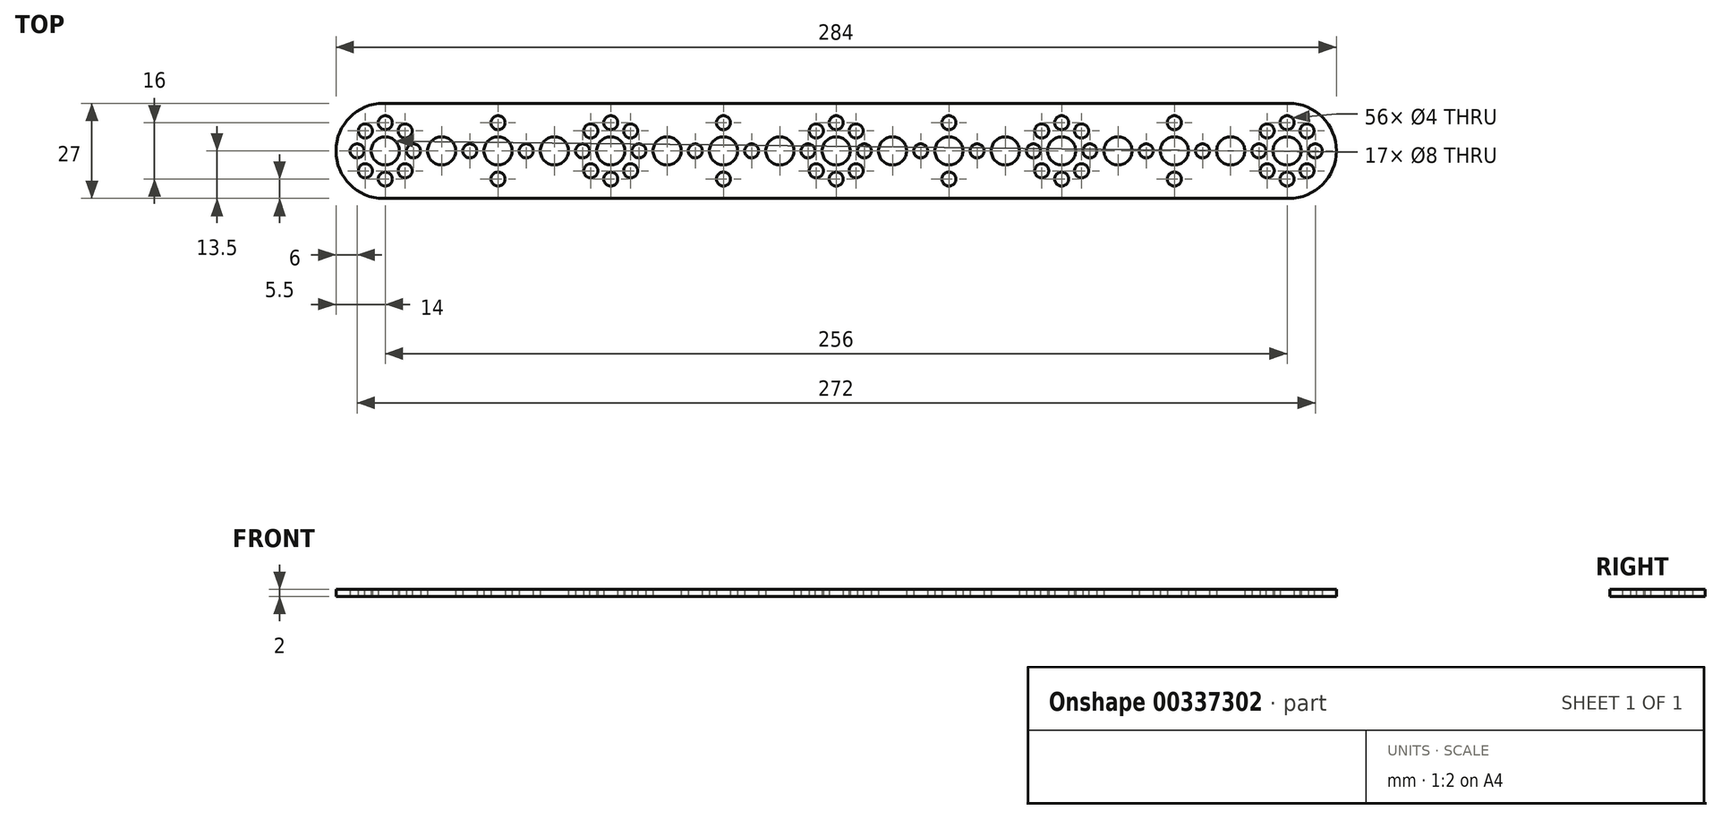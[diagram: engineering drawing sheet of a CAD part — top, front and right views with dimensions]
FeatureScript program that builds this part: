
annotation { "Feature Type Name" : "Feature", "Feature Type Description" : "" }
export const myFeature = defineFeature(function(context is Context, id is Id, definition is map)
    precondition{}
    {
        {
            var Q0;
            Q0=qCreatedBy(makeId("Top.planeOp"),FACE);
            var sketch = newSketch(context, id + "F0", { "sketchPlane" : qUnion([Q0])});
            skLineSegment(sketch, "E0.bottom", {"start": v(128.5, 13.5) * mm, "end": v(-128.5, 13.5) * mm});
            skLineSegment(sketch, "E0.top", {"start": v(128.5, -13.5) * mm, "end": v(-128.5, -13.5) * mm});
            skLineSegment(sketch, "E0.left", {"start": v(128.5, 13.5) * mm, "end": v(128.5, -13.5) * mm});
            skLineSegment(sketch, "E0.right", {"start": v(-128.5, 13.5) * mm, "end": v(-128.5, -13.5) * mm});
            skPoint(sketch, "E0.middle", {"position": v(0, 0) * mm});
            skArc(sketch, "E1", {"start": v(-128.5, 13.5) * mm, "mid": v(-142, 0) * mm, "end": v(-128.5, -13.5) * mm});
            skArc(sketch, "E2", {"start": v(128.5, -13.5) * mm, "mid": v(142, 0) * mm, "end": v(128.5, 13.5) * mm});
            skLineSegment(sketch, "E3", {"start": v(-128, 2.64) * mm, "end": v(-128, 0) * mm});
            skLineSegment(sketch, "E4", {"start": v(-128, 0) * mm, "end": v(-128, -2.64) * mm});
            skLineSegment(sketch, "E5", {"start": v(-132, 0) * mm, "end": v(-128, 0) * mm});
            skLineSegment(sketch, "E6", {"start": v(-126.43, 0) * mm, "end": v(-128, 0) * mm});
            skLineSegment(sketch, "E7", {"start": v(-128, 0) * mm, "end": v(-126.72, 1.28) * mm});
            skLineSegment(sketch, "E8", {"start": v(-128, 0) * mm, "end": v(-129.4, -1.4) * mm});
            skLineSegment(sketch, "E9", {"start": v(-128, 0) * mm, "end": v(-129.4, 1.4) * mm});
            skLineSegment(sketch, "E10", {"start": v(-128, 0) * mm, "end": v(-126.62, -1.38) * mm});
            skCircle(sketch, "E11", {"center": v(-128, 0) * mm, "radius": 4 * mm});
            skCircle(sketch, "E12", {"center": v(-133.66, 5.66) * mm, "radius": 2 * mm});
            skCircle(sketch, "E13", {"center": v(-128, 8) * mm, "radius": 2 * mm});
            skCircle(sketch, "E14", {"center": v(-122.34, 5.66) * mm, "radius": 2 * mm});
            skCircle(sketch, "E15", {"center": v(-120, 0) * mm, "radius": 2 * mm});
            skCircle(sketch, "E16", {"center": v(-136, 0) * mm, "radius": 2 * mm});
            skCircle(sketch, "E17", {"center": v(-133.66, -5.66) * mm, "radius": 2 * mm});
            skCircle(sketch, "E18", {"center": v(-128, -8) * mm, "radius": 2 * mm});
            skCircle(sketch, "E19", {"center": v(-122.34, -5.66) * mm, "radius": 2 * mm});
            skCircle(sketch, "E20", {"center": v(-112, 0) * mm, "radius": 4 * mm});
            skCircle(sketch, "E21", {"center": v(-96, 0) * mm, "radius": 4 * mm});
            skCircle(sketch, "E22", {"center": v(-96, 8) * mm, "radius": 2 * mm});
            skCircle(sketch, "E23", {"center": v(-88, 0) * mm, "radius": 2 * mm});
            skCircle(sketch, "E24", {"center": v(-96, -8) * mm, "radius": 2 * mm});
            skCircle(sketch, "E25", {"center": v(-104, 0) * mm, "radius": 2 * mm});
            skCircle(sketch, "E26", {"center": v(-80, 0) * mm, "radius": 4 * mm});
            skLineSegment(sketch, "E27", {"start": v(-64, 2.64) * mm, "end": v(-64, 0) * mm});
            skLineSegment(sketch, "E28", {"start": v(-64, 0) * mm, "end": v(-64, -2.64) * mm});
            skLineSegment(sketch, "E29", {"start": v(-65.19, 0) * mm, "end": v(-64, 0) * mm});
            skLineSegment(sketch, "E30", {"start": v(-59.62, 0) * mm, "end": v(-64, 0) * mm});
            skLineSegment(sketch, "E31", {"start": v(-64, 0) * mm, "end": v(-62.72, 1.28) * mm});
            skLineSegment(sketch, "E32", {"start": v(-64, 0) * mm, "end": v(-65.4, -1.4) * mm});
            skLineSegment(sketch, "E33", {"start": v(-64, 0) * mm, "end": v(-65.4, 1.4) * mm});
            skLineSegment(sketch, "E34", {"start": v(-64, 0) * mm, "end": v(-62.62, -1.38) * mm});
            skCircle(sketch, "E35", {"center": v(-64, 0) * mm, "radius": 4 * mm});
            skCircle(sketch, "E36", {"center": v(-69.66, 5.66) * mm, "radius": 2 * mm});
            skCircle(sketch, "E37", {"center": v(-64, 8) * mm, "radius": 2 * mm});
            skCircle(sketch, "E38", {"center": v(-58.34, 5.66) * mm, "radius": 2 * mm});
            skCircle(sketch, "E39", {"center": v(-56, 0) * mm, "radius": 2 * mm});
            skCircle(sketch, "E40", {"center": v(-72, 0) * mm, "radius": 2 * mm});
            skCircle(sketch, "E41", {"center": v(-69.66, -5.66) * mm, "radius": 2 * mm});
            skCircle(sketch, "E42", {"center": v(-64, -8) * mm, "radius": 2 * mm});
            skCircle(sketch, "E43", {"center": v(-58.34, -5.66) * mm, "radius": 2 * mm});
            skCircle(sketch, "E44", {"center": v(-48, 0) * mm, "radius": 4 * mm});
            skCircle(sketch, "E45", {"center": v(-32, 0) * mm, "radius": 4 * mm});
            skCircle(sketch, "E46", {"center": v(-32, 8) * mm, "radius": 2 * mm});
            skCircle(sketch, "E47", {"center": v(-24, 0) * mm, "radius": 2 * mm});
            skCircle(sketch, "E48", {"center": v(-32, -8) * mm, "radius": 2 * mm});
            skCircle(sketch, "E49", {"center": v(-40, 0) * mm, "radius": 2 * mm});
            skCircle(sketch, "E50", {"center": v(-16, 0) * mm, "radius": 4 * mm});
            skCircle(sketch, "E51.MirrorC", {"center": v(16, 0) * mm, "radius": 4 * mm});
            skCircle(sketch, "E52.MirrorC", {"center": v(24, 0) * mm, "radius": 2 * mm});
            skCircle(sketch, "E53.MirrorC", {"center": v(32, 0) * mm, "radius": 4 * mm});
            skCircle(sketch, "E54.MirrorC", {"center": v(32, 8) * mm, "radius": 2 * mm});
            skCircle(sketch, "E55.MirrorC", {"center": v(40, 0) * mm, "radius": 2 * mm});
            skCircle(sketch, "E56.MirrorC", {"center": v(32, -8) * mm, "radius": 2 * mm});
            skCircle(sketch, "E57.MirrorC", {"center": v(48, 0) * mm, "radius": 4 * mm});
            skCircle(sketch, "E58.MirrorC", {"center": v(64, -8) * mm, "radius": 2 * mm});
            skCircle(sketch, "E59.MirrorC", {"center": v(58.34, -5.66) * mm, "radius": 2 * mm});
            skCircle(sketch, "E60.MirrorC", {"center": v(56, 0) * mm, "radius": 2 * mm});
            skCircle(sketch, "E61.MirrorC", {"center": v(58.34, 5.66) * mm, "radius": 2 * mm});
            skCircle(sketch, "E62.MirrorC", {"center": v(64, 8) * mm, "radius": 2 * mm});
            skCircle(sketch, "E63.MirrorC", {"center": v(69.66, 5.66) * mm, "radius": 2 * mm});
            skCircle(sketch, "E64.MirrorC", {"center": v(72, 0) * mm, "radius": 2 * mm});
            skCircle(sketch, "E65.MirrorC", {"center": v(69.66, -5.66) * mm, "radius": 2 * mm});
            skCircle(sketch, "E66.MirrorC", {"center": v(64, 0) * mm, "radius": 4 * mm});
            skCircle(sketch, "E67.MirrorC", {"center": v(80, 0) * mm, "radius": 4 * mm});
            skCircle(sketch, "E68.MirrorC", {"center": v(88, 0) * mm, "radius": 2 * mm});
            skCircle(sketch, "E69.MirrorC", {"center": v(96, 0) * mm, "radius": 4 * mm});
            skCircle(sketch, "E70.MirrorC", {"center": v(96, -8) * mm, "radius": 2 * mm});
            skCircle(sketch, "E71.MirrorC", {"center": v(96, 8) * mm, "radius": 2 * mm});
            skCircle(sketch, "E72.MirrorC", {"center": v(104, 0) * mm, "radius": 2 * mm});
            skCircle(sketch, "E73.MirrorC", {"center": v(112, 0) * mm, "radius": 4 * mm});
            skCircle(sketch, "E74.MirrorC", {"center": v(128, -8) * mm, "radius": 2 * mm});
            skCircle(sketch, "E75.MirrorC", {"center": v(122.34, -5.66) * mm, "radius": 2 * mm});
            skCircle(sketch, "E76.MirrorC", {"center": v(120, 0) * mm, "radius": 2 * mm});
            skCircle(sketch, "E77.MirrorC", {"center": v(122.34, 5.66) * mm, "radius": 2 * mm});
            skCircle(sketch, "E78.MirrorC", {"center": v(128, 8) * mm, "radius": 2 * mm});
            skCircle(sketch, "E79.MirrorC", {"center": v(133.66, 5.66) * mm, "radius": 2 * mm});
            skCircle(sketch, "E80.MirrorC", {"center": v(133.66, -5.66) * mm, "radius": 2 * mm});
            skCircle(sketch, "E81.MirrorC", {"center": v(128, 0) * mm, "radius": 4 * mm});
            skCircle(sketch, "E82.MirrorC", {"center": v(136, 0) * mm, "radius": 2 * mm});
            skLineSegment(sketch, "E83", {"start": v(0, 2.64) * mm, "end": v(0, 0) * mm});
            skLineSegment(sketch, "E84", {"start": v(0, 0) * mm, "end": v(0, -2.64) * mm});
            skLineSegment(sketch, "E85", {"start": v(-1.19, 0) * mm, "end": v(0, 0) * mm});
            skLineSegment(sketch, "E86", {"start": v(4.38, 0) * mm, "end": v(0, 0) * mm});
            skLineSegment(sketch, "E87", {"start": v(0, 0) * mm, "end": v(1.28, 1.28) * mm});
            skLineSegment(sketch, "E88", {"start": v(0, 0) * mm, "end": v(-1.4, -1.4) * mm});
            skLineSegment(sketch, "E89", {"start": v(0, 0) * mm, "end": v(-1.4, 1.4) * mm});
            skLineSegment(sketch, "E90", {"start": v(0, 0) * mm, "end": v(1.38, -1.38) * mm});
            skCircle(sketch, "E91", {"center": v(0, 0) * mm, "radius": 4 * mm});
            skCircle(sketch, "E92", {"center": v(-5.66, 5.66) * mm, "radius": 2 * mm});
            skCircle(sketch, "E93", {"center": v(0, 8) * mm, "radius": 2 * mm});
            skCircle(sketch, "E94", {"center": v(5.66, 5.66) * mm, "radius": 2 * mm});
            skCircle(sketch, "E95", {"center": v(8, 0) * mm, "radius": 2 * mm});
            skCircle(sketch, "E96", {"center": v(-8, 0) * mm, "radius": 2 * mm});
            skCircle(sketch, "E97", {"center": v(-5.66, -5.66) * mm, "radius": 2 * mm});
            skCircle(sketch, "E98", {"center": v(0, -8) * mm, "radius": 2 * mm});
            skCircle(sketch, "E99", {"center": v(5.66, -5.66) * mm, "radius": 2 * mm});
            skSolve(sketch);
        }
        {
            var Q0;
            {var subQ8=sQuery(id+"F0.wireOp",EDGE,"E0.bottom");Q0=makeQuery(id+"F0.imprint","IMPRINT",FACE,{"disambiguationData":[TD([[makeQuery(id+"F0.imprint","IMPRINT",EDGE,{"derivedFrom":subQ8}),1.0]])]});}
            var Q1;
            {var subQ0=sQuery(id+"F0.wireOp",EDGE,"E1");Q1=makeQuery(id+"F0.imprint","IMPRINT",FACE,{"disambiguationData":[TD([[makeQuery(id+"F0.imprint","IMPRINT",EDGE,{"derivedFrom":subQ0}),1.0]])]});}
            var Q2;
            {var subQ4=sQuery(id+"F0.wireOp",EDGE,"E2");Q2=makeQuery(id+"F0.imprint","IMPRINT",FACE,{"disambiguationData":[TD([[makeQuery(id+"F0.imprint","IMPRINT",EDGE,{"derivedFrom":subQ4}),1.0]])]});}
            extrude(context, id + "F1", {"entities" : qUnion([Q0, Q1, Q2]), "depth" : 2 * mm});
        }
    });
